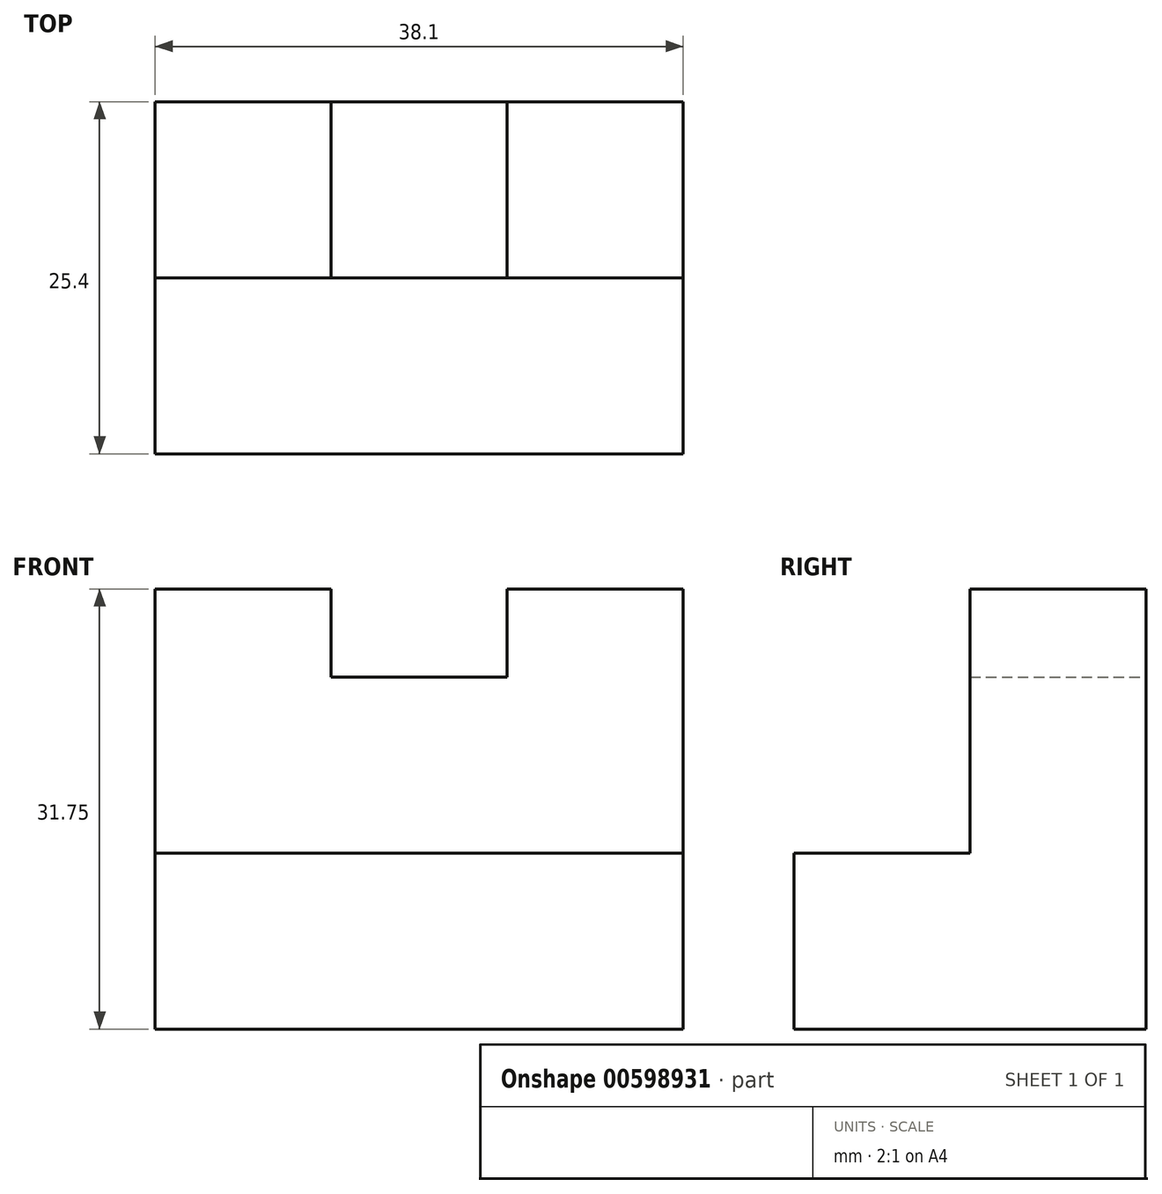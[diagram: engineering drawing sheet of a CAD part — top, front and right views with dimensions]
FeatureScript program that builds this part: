
annotation { "Feature Type Name" : "Feature", "Feature Type Description" : "" }
export const myFeature = defineFeature(function(context is Context, id is Id, definition is map)
    precondition{}
    {
        {
            var Q0;
            Q0=qCreatedBy(makeId("Front.planeOp"),FACE);
            var sketch = newSketch(context, id + "F0", { "sketchPlane" : qUnion([Q0])});
            skLineSegment(sketch, "E0", {"start": v(0, 0) * mm, "end": v(0, 12.7) * mm});
            skLineSegment(sketch, "E1", {"start": v(0, 12.7) * mm, "end": v(0, 31.75) * mm});
            skLineSegment(sketch, "E2", {"start": v(0, 31.75) * mm, "end": v(12.7, 31.75) * mm});
            skLineSegment(sketch, "E3", {"start": v(12.7, 31.75) * mm, "end": v(12.7, 25.4) * mm});
            skLineSegment(sketch, "E4", {"start": v(12.7, 25.4) * mm, "end": v(25.4, 25.4) * mm});
            skLineSegment(sketch, "E5", {"start": v(25.4, 25.4) * mm, "end": v(25.4, 31.75) * mm});
            skLineSegment(sketch, "E6", {"start": v(25.4, 31.75) * mm, "end": v(38.1, 31.75) * mm});
            skLineSegment(sketch, "E7", {"start": v(38.1, 31.75) * mm, "end": v(38.1, 12.7) * mm});
            skLineSegment(sketch, "E8", {"start": v(38.1, 12.7) * mm, "end": v(38.1, 0) * mm});
            skLineSegment(sketch, "E9", {"start": v(38.1, 0) * mm, "end": v(0, 0) * mm});
            skSolve(sketch);
        }
        {
            var Q0;
            Q0 = qSketchRegion(id + "F0", true);
            extrude(context, id + "F1", {"entities" : qUnion([Q0]), "depth" : 12.7 * mm, "offsetDistance" : 25.4 * mm});
        }
        {
            var Q0;
            Q0=qCreatedBy(makeId("Right.planeOp"),FACE);
            var sketch = newSketch(context, id + "F2", { "sketchPlane" : qUnion([Q0])});
            skLineSegment(sketch, "E10", {"start": v(0, 0) * mm, "end": v(-25.4, 0) * mm});
            skLineSegment(sketch, "E11", {"start": v(-25.4, 0) * mm, "end": v(-25.4, 12.7) * mm});
            skLineSegment(sketch, "E12", {"start": v(-25.4, 12.7) * mm, "end": v(-12.7, 12.7) * mm});
            skLineSegment(sketch, "E13", {"start": v(-12.7, 12.7) * mm, "end": v(-12.7, 0) * mm});
            skSolve(sketch);
        }
        {
            var Q0;
            Q0 = qSketchRegion(id + "F2", true);
            extrude(context, id + "F3", {"entities" : qUnion([Q0]), "operationType" : NewBodyOperationType.ADD, "depth" : 12.7 * mm, "offsetDistance" : 25.4 * mm});
        }
        {
            var Q0;
            Q0=qCreatedBy(makeId("Top.planeOp"),FACE);
            var sketch = newSketch(context, id + "F4", { "sketchPlane" : qUnion([Q0])});
            skLineSegment(sketch, "E14", {"start": v(0, 0) * mm, "end": v(0, -25.4) * mm});
            skLineSegment(sketch, "E15", {"start": v(0, -25.4) * mm, "end": v(38.1, -25.4) * mm});
            skLineSegment(sketch, "E16", {"start": v(38.1, -25.4) * mm, "end": v(38.1, -12.7) * mm});
            skLineSegment(sketch, "E17", {"start": v(38.1, -12.7) * mm, "end": v(0, -12.7) * mm});
            skSolve(sketch);
        }
        {
            var Q0;
            Q0 = qSketchRegion(id + "F4", true);
            extrude(context, id + "F5", {"entities" : qUnion([Q0]), "operationType" : NewBodyOperationType.ADD, "depth" : 12.7 * mm, "offsetDistance" : 25.4 * mm});
        }
    });
